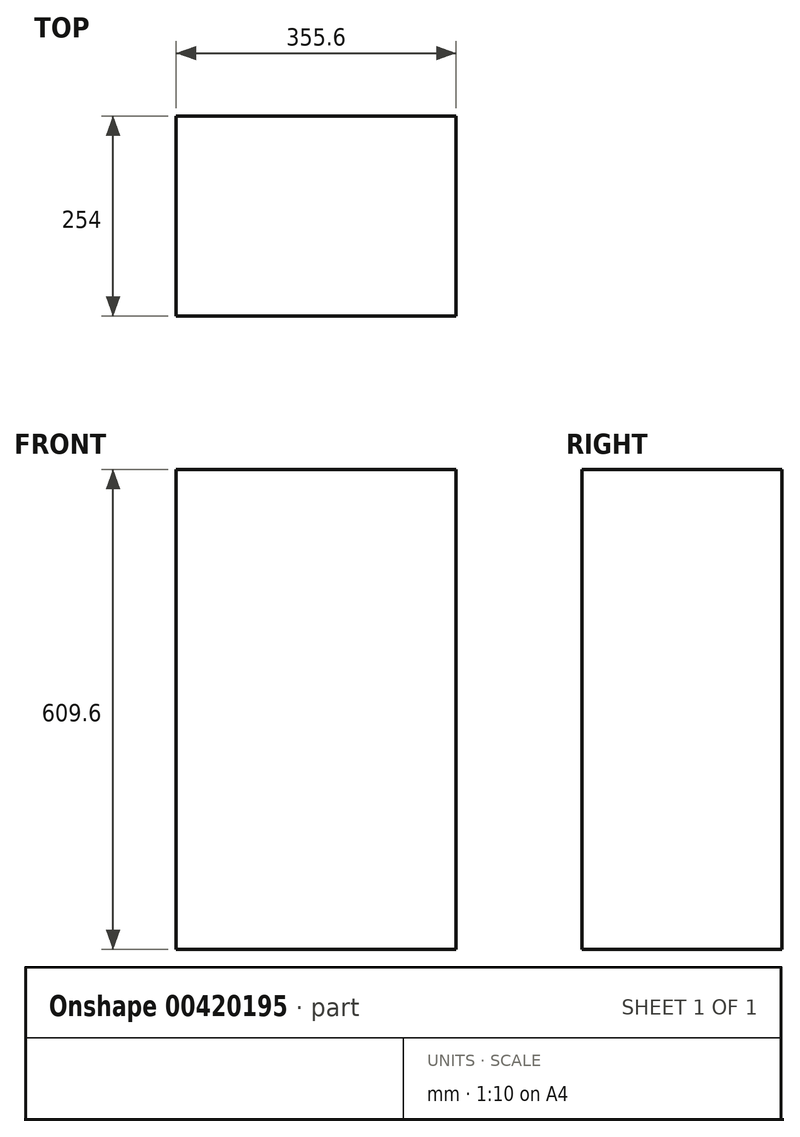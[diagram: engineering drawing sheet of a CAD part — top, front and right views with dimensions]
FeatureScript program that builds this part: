
annotation { "Feature Type Name" : "Feature", "Feature Type Description" : "" }
export const myFeature = defineFeature(function(context is Context, id is Id, definition is map)
    precondition{}
    {
        {
            var Q0;
            Q0=qCreatedBy(makeId("Front.planeOp"),FACE);
            var sketch = newSketch(context, id + "F0", { "sketchPlane" : qUnion([Q0])});
            skLineSegment(sketch, "E0.bottom", {"start": v(0, 0) * mm, "end": v(355.6, 0) * mm});
            skLineSegment(sketch, "E0.top", {"start": v(0, 609.6) * mm, "end": v(355.6, 609.6) * mm});
            skLineSegment(sketch, "E0.left", {"start": v(0, 0) * mm, "end": v(0, 609.6) * mm});
            skLineSegment(sketch, "E0.right", {"start": v(355.6, 0) * mm, "end": v(355.6, 609.6) * mm});
            skSolve(sketch);
        }
        {
            var Q0;
            Q0 = qSketchRegion(id + "F0", true);
            extrude(context, id + "F1", {"entities" : qUnion([Q0]), "depth" : 254 * mm});
        }
    });
